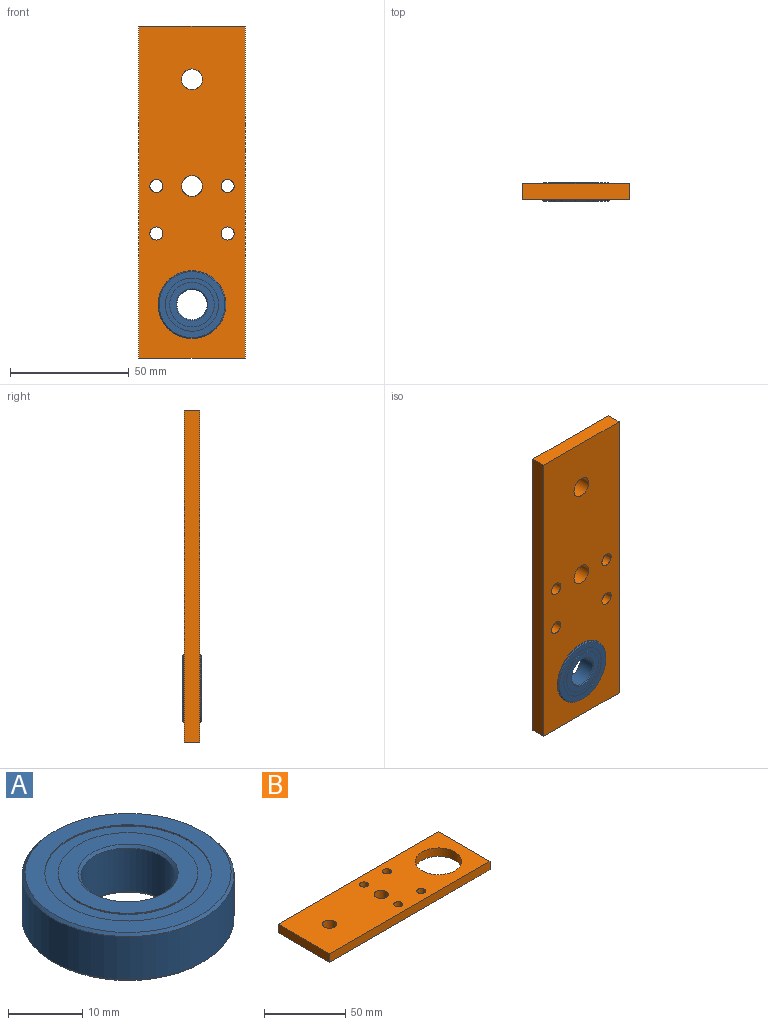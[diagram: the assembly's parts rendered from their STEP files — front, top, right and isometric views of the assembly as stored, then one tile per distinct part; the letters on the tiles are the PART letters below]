
ASSEMBLY  parts=2 mates=1
PART A: 24 faces, bbox 28.6x28.6x7.9 mm
  f0: plane 22.45x22.45mm, normal (0,0,-1), area 117.6mm2, adj f1,f8
  f1: cylinder r=9.41mm len=18.82mm, axis (0,0,1), area 11.7mm2, adj f0,f7
  f2: cone r=6.75mm half-angle=45deg, axis (0,0,1), area 23.1mm2, adj f3,f6
  f3: cylinder r=6.35mm len=12.7mm, axis (0,0,1), area 285mm2, adj f2,f4
  f4: cone r=6.35mm half-angle=45deg, axis (0,0,-1), area 23.1mm2, adj f3,f7
  f5: cylinder r=9.41mm len=18.82mm, axis (0,0,1), area 11.7mm2, adj f6,f15
  f6: plane 18.82x18.82mm, normal (0,0,1), area 135.3mm2, adj f2,f5
  f7: plane 18.82x18.82mm, normal (0,0,-1), area 135.3mm2, adj f1,f4
  f8: cylinder r=11.23mm len=22.45mm, axis (0,0,1), area 14mm2, adj f0,f13
  f9: cylinder r=11.23mm len=22.45mm, axis (0,0,1), area 14mm2, adj f14,f15
  f10: cone r=13.89mm half-angle=45deg, axis (0,0,1), area 49.7mm2, adj f11,f13
  f11: cylinder r=14.29mm len=28.58mm, axis (0,0,1), area 641.3mm2, adj f10,f12
  f12: cone r=14.29mm half-angle=45deg, axis (0,0,-1), area 49.7mm2, adj f11,f14
  f13: plane 27.78x27.78mm, normal (0,0,-1), area 210.3mm2, adj f8,f10
  f14: plane 27.78x27.78mm, normal (0,0,1), area 210.3mm2, adj f9,f12
  f15: plane 22.45x22.45mm, normal (0,0,1), area 117.6mm2, adj f5,f9
  f16: plane 22.45x22.45mm, normal (0,0,-1), area 117.6mm2, adj f19,f23
  f17: cylinder r=11.23mm len=22.45mm, axis (0,0,1), area 15.5mm2, adj f18,f20
  f18: torus R=10.32mm, axis (0,0,1), area 325.8mm2, adj f17,f19
  f19: cylinder r=11.23mm len=22.45mm, axis (0,0,1), area 15.5mm2, adj f16,f18
  f20: plane 22.45x22.45mm, normal (0,0,1), area 117.6mm2, adj f17,f21
  f21: cylinder r=9.41mm len=18.82mm, axis (0,0,1), area 13mm2, adj f20,f22
  f22: torus R=10.32mm, axis (0,0,1), area 237.9mm2, adj f21,f23
  f23: cylinder r=9.41mm len=18.82mm, axis (0,0,1), area 13mm2, adj f16,f22
PART B: 13 faces, bbox 140x45x6.4 mm
  f0: plane 140x6.4mm, normal (0,1,0), area 896mm2, adj f1,f4,f5,f6
  f1: plane 45x6.4mm, normal (-1,0,0), area 288mm2, adj f0,f2,f5,f6
  f2: plane 140x6.4mm, normal (0,-1,0), area 896mm2, adj f1,f4,f5,f6
  f3: cylinder r=14.29mm len=28.58mm, axis (0,0,-1), area 574.5mm2, adj f5,f6
  f4: plane 45x6.4mm, normal (1,0,0), area 288mm2, adj f0,f2,f5,f6
  f5: plane 140x45mm, normal (0,0,1), area 5442mm2, adj f0,f1,f2,f3,f4,f7,f8,f9
  f6: plane 140x45mm, normal (0,0,-1), area 5442mm2, adj f0,f1,f2,f3,f4,f7,f8,f9
  f7: cylinder r=4.4mm len=8.8mm, axis (0,0,-1), area 176.9mm2, adj f5,f6
  f8: cylinder r=4.4mm len=8.8mm, axis (0,0,-1), area 176.9mm2, adj f5,f6
  f9: cylinder r=2.75mm len=6.4mm, axis (0,0,-1), area 110.6mm2, adj f5,f6
  f10: cylinder r=2.75mm len=6.4mm, axis (0,0,-1), area 110.6mm2, adj f5,f6
  f11: cylinder r=2.75mm len=6.4mm, axis (0,0,-1), area 110.6mm2, adj f5,f6
  f12: cylinder r=2.75mm len=6.4mm, axis (0,0,-1), area 110.6mm2, adj f5,f6
PLACE A rot(axis=(0,-0.71,0.71),180deg) t=(0,-3.2,0)mm
PLACE B rot(axis=(-0.58,0.58,0.58),120deg) t=(0,-6.4,47.5)mm
MATE fastened A.f1 <-> B.f3  axis (0,-1,0) through (0,-3.2,0)mm
